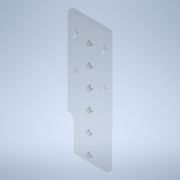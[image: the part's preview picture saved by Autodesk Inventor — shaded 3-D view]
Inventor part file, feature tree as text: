
AUTODESK INVENTOR PART (.ipt)
format: ipt  version: 2022 (Build 260153000, 153)  size: 187,392 bytes
history: native  units: mm
features: thread x6, sketch x2, extrude x2, hole x1, chamfer x1, plane x1, other x1
ambient origin geometry x8: Origin, YZ Plane, XZ Plane, XY Plane, X Axis, Y Axis, Z Axis, Center Point
bodies: Solid1 (feature_tree)
feature tree (14):
  sketch  "Sketch1"  dims[d0=5.5mm d1=76.5mm]
  extrude  "Extrusion1"  Depth=76.5mm
  hole  "Hole1"  [1 undecoded]
  extrude  "Extrusion2"  Depth=4.0mm
  chamfer  "Chamfer1"  Distance=3.8mm
  thread  "Thread1"  [1 undecoded]
  thread  "Thread2"  [1 undecoded]
  thread  "Thread3"  [1 undecoded]
  thread  "Thread4"  [1 undecoded]
  thread  "Thread5"  [1 undecoded]
  thread  "Thread6"  [1 undecoded]
  plane  "Work Plane1"
  sketch  "Sketch2"  dims[d2=35.0mm d3=106.5mm d5=17.5mm d6=3.8mm d7=60.0mm d9=17.0mm d10=10.0mm d12=10.0mm d14=85.0mm d15=4.0mm d16=6.6mm d17=3.2mm d18=20.0mm d20=30.0mm d21=10.0mm d23=10.0mm d25=30.0mm d26=4.5mm d27=0.0mm d28=3.2mm d29=6.0mm d30=6.6mm d31=2.0mm d32=90.0deg d33=8.0mm d34=20.594885mm d35=4.0mm d36=0.0mm d37=0.5mm d38=2.0mm d39=45.0deg d40=4.0mm d41=0.0mm d42=4.0mm d43=0.0mm d44=4.0mm d45=0.0mm d46=3.5mm d47=0.0mm d48=3.5mm d49=0.0mm d50=4.0mm d51=0.0mm d52=90.0deg d53=5.0mm d54=15.0mm]
  other  "Work Axis1"
note: 7 required parameter values undecoded (feature->parameter linkage not recoverable at this tier; creation-order binding heuristic only, values carry confidence <= 0.55)
